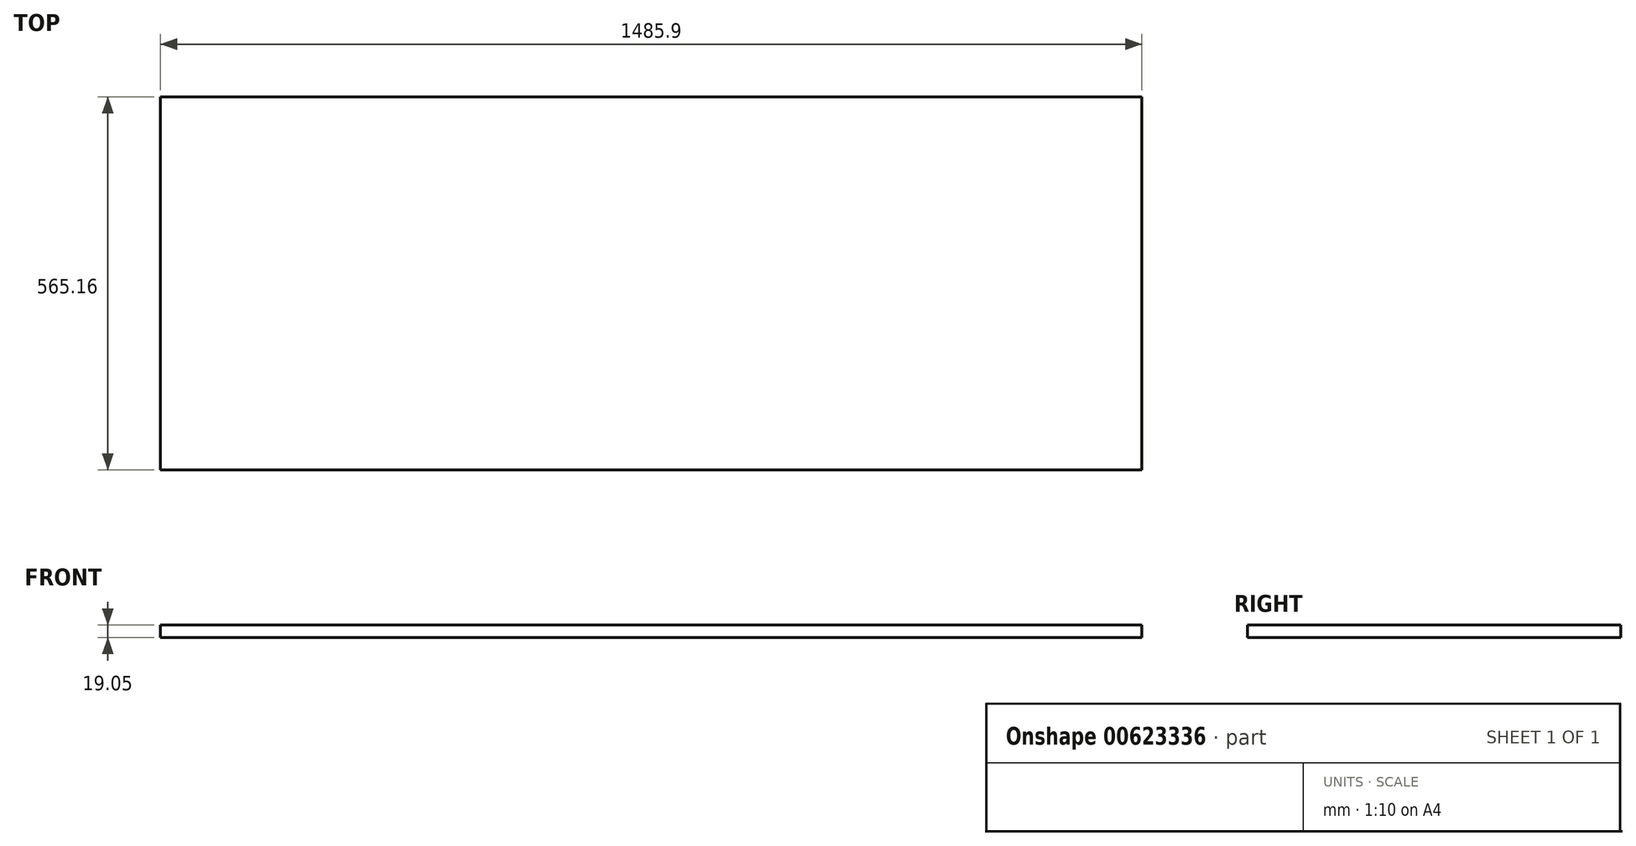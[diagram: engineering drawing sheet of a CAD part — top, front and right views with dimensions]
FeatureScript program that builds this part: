
annotation { "Feature Type Name" : "Feature", "Feature Type Description" : "" }
export const myFeature = defineFeature(function(context is Context, id is Id, definition is map)
    precondition{}
    {
        {
            var Q0;
            Q0=qCreatedBy(makeId("Top.planeOp"),FACE);
            var sketch = newSketch(context, id + "F0", { "sketchPlane" : qUnion([Q0])});
            skLineSegment(sketch, "E0.bottom", {"start": v(-742.95, 282.58) * mm, "end": v(742.95, 282.58) * mm});
            skLineSegment(sketch, "E0.top", {"start": v(-742.95, -282.57) * mm, "end": v(742.95, -282.57) * mm});
            skLineSegment(sketch, "E0.left", {"start": v(-742.95, 282.58) * mm, "end": v(-742.95, -282.57) * mm});
            skLineSegment(sketch, "E0.right", {"start": v(742.95, 282.58) * mm, "end": v(742.95, -282.57) * mm});
            skPoint(sketch, "E0.middle", {"position": v(0, 0) * mm});
            skSolve(sketch);
        }
        {
            var Q0;
            Q0=makeQuery(id+"F0.imprint","IMPRINT",FACE,{"disambiguationData":[TD([[makeQuery(id+"F0.imprint","IMPRINT",EDGE,{"derivedFrom":sQuery(id+"F0.wireOp",EDGE,"E0.bottom")}),-1.0]])]});
            extrude(context, id + "F1", {"entities" : qUnion([Q0]), "depth" : 19.05 * mm, "offsetDistance" : 25.4 * mm});
        }
    });
